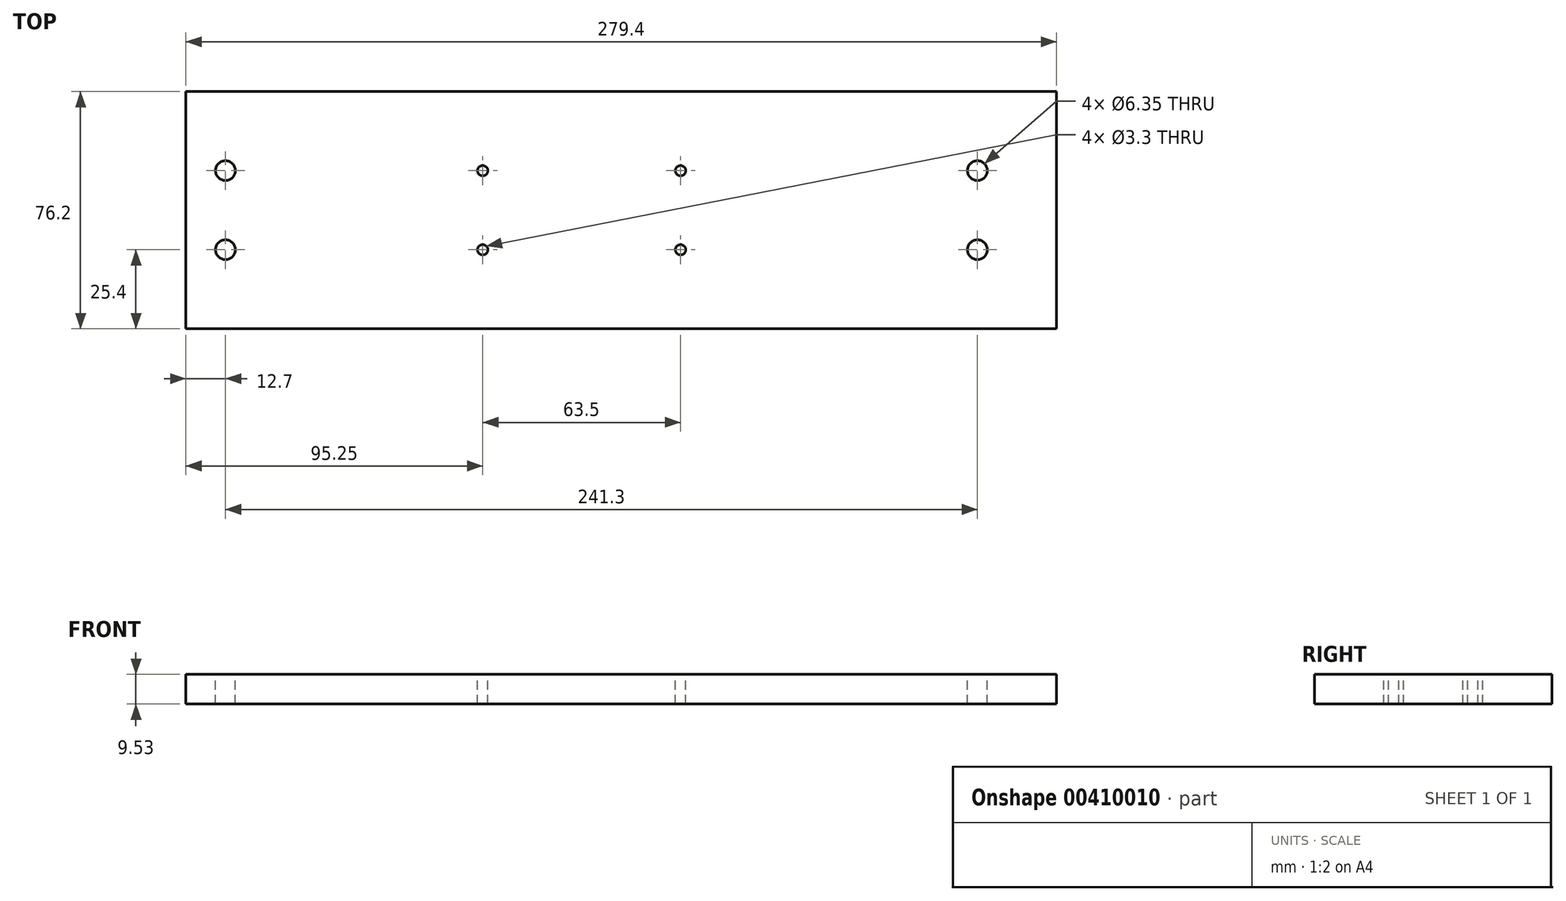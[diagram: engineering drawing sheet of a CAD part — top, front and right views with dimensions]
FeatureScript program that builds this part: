
annotation { "Feature Type Name" : "Feature", "Feature Type Description" : "" }
export const myFeature = defineFeature(function(context is Context, id is Id, definition is map)
    precondition{}
    {
        {
            var Q0;
            Q0=qCreatedBy(makeId("Top.planeOp"),FACE);
            var sketch = newSketch(context, id + "F0", { "sketchPlane" : qUnion([Q0])});
            skLineSegment(sketch, "E0.bottom", {"start": v(139.7, 38.1) * mm, "end": v(-139.7, 38.1) * mm});
            skLineSegment(sketch, "E0.top", {"start": v(139.7, -38.1) * mm, "end": v(-139.7, -38.1) * mm});
            skLineSegment(sketch, "E0.left", {"start": v(139.7, 38.1) * mm, "end": v(139.7, -38.1) * mm});
            skLineSegment(sketch, "E0.right", {"start": v(-139.7, 38.1) * mm, "end": v(-139.7, -38.1) * mm});
            skPoint(sketch, "E0.middle", {"position": v(0, 0) * mm});
            skSolve(sketch);
        }
        {
            var Q0;
            Q0=makeQuery(id+"F0.imprint","IMPRINT",FACE,{"disambiguationData":[TD([[makeQuery(id+"F0.imprint","IMPRINT",EDGE,{"derivedFrom":sQuery(id+"F0.wireOp",EDGE,"E0.bottom")}),1.0]])]});
            extrude(context, id + "F1", {"entities" : qUnion([Q0]), "depth" : 9.52 * mm});
        }
        {
            var Q0;
            Q0=makeQuery(id+"F1.opExtrude","CAP_FACE",FACE,{"disambiguationData":[OSD([sQuery(id+"F0.wireOp",EDGE,"E0.bottom"),sQuery(id+"F0.wireOp",EDGE,"E0.top"),sQuery(id+"F0.wireOp",EDGE,"E0.left"),sQuery(id+"F0.wireOp",EDGE,"E0.right")])],"isStart":false});
            var sketch = newSketch(context, id + "F2", { "sketchPlane" : qUnion([Q0])});
            skCircle(sketch, "E1", {"center": v(-127, 12.7) * mm, "radius": 3.18 * mm});
            skCircle(sketch, "E2", {"center": v(-127, -12.7) * mm, "radius": 3.18 * mm});
            skCircle(sketch, "E3", {"center": v(-44.45, 12.7) * mm, "radius": 1.65 * mm});
            skCircle(sketch, "E4", {"center": v(-44.45, -12.7) * mm, "radius": 1.65 * mm});
            skCircle(sketch, "E5", {"center": v(19.05, 12.7) * mm, "radius": 1.65 * mm});
            skCircle(sketch, "E6", {"center": v(19.05, -12.7) * mm, "radius": 1.65 * mm});
            skCircle(sketch, "E7", {"center": v(114.3, 12.7) * mm, "radius": 3.18 * mm});
            skCircle(sketch, "E8", {"center": v(114.3, -12.7) * mm, "radius": 3.18 * mm});
            skSolve(sketch);
        }
        {
            var Q0;
            Q0=makeQuery(id+"F2.imprint","IMPRINT",FACE,{"disambiguationData":[TD([[makeQuery(id+"F2.imprint","IMPRINT",EDGE,{"derivedFrom":sQuery(id+"F2.wireOp",EDGE,"E8")}),1.0]])]});
            var Q1;
            Q1=makeQuery(id+"F2.imprint","IMPRINT",FACE,{"disambiguationData":[TD([[makeQuery(id+"F2.imprint","IMPRINT",EDGE,{"derivedFrom":sQuery(id+"F2.wireOp",EDGE,"E7")}),1.0]])]});
            var Q2;
            Q2=makeQuery(id+"F2.imprint","IMPRINT",FACE,{"disambiguationData":[TD([[makeQuery(id+"F2.imprint","IMPRINT",EDGE,{"derivedFrom":sQuery(id+"F2.wireOp",EDGE,"E5")}),1.0]])]});
            var Q3;
            Q3=makeQuery(id+"F2.imprint","IMPRINT",FACE,{"disambiguationData":[TD([[makeQuery(id+"F2.imprint","IMPRINT",EDGE,{"derivedFrom":sQuery(id+"F2.wireOp",EDGE,"E6")}),1.0]])]});
            var Q4;
            Q4=makeQuery(id+"F2.imprint","IMPRINT",FACE,{"disambiguationData":[TD([[makeQuery(id+"F2.imprint","IMPRINT",EDGE,{"derivedFrom":sQuery(id+"F2.wireOp",EDGE,"E3")}),1.0]])]});
            var Q5;
            Q5=makeQuery(id+"F2.imprint","IMPRINT",FACE,{"disambiguationData":[TD([[makeQuery(id+"F2.imprint","IMPRINT",EDGE,{"derivedFrom":sQuery(id+"F2.wireOp",EDGE,"E4")}),1.0]])]});
            var Q6;
            Q6=makeQuery(id+"F2.imprint","IMPRINT",FACE,{"disambiguationData":[TD([[makeQuery(id+"F2.imprint","IMPRINT",EDGE,{"derivedFrom":sQuery(id+"F2.wireOp",EDGE,"E1")}),1.0]])]});
            var Q7;
            Q7=makeQuery(id+"F2.imprint","IMPRINT",FACE,{"disambiguationData":[TD([[makeQuery(id+"F2.imprint","IMPRINT",EDGE,{"derivedFrom":sQuery(id+"F2.wireOp",EDGE,"E2")}),1.0]])]});
            extrude(context, id + "F3", {"entities" : qUnion([Q0, Q1, Q2, Q3, Q4, Q5, Q6, Q7]), "operationType" : NewBodyOperationType.REMOVE, "oppositeDirection" : true, "depth" : 25.4 * mm});
        }
    });
